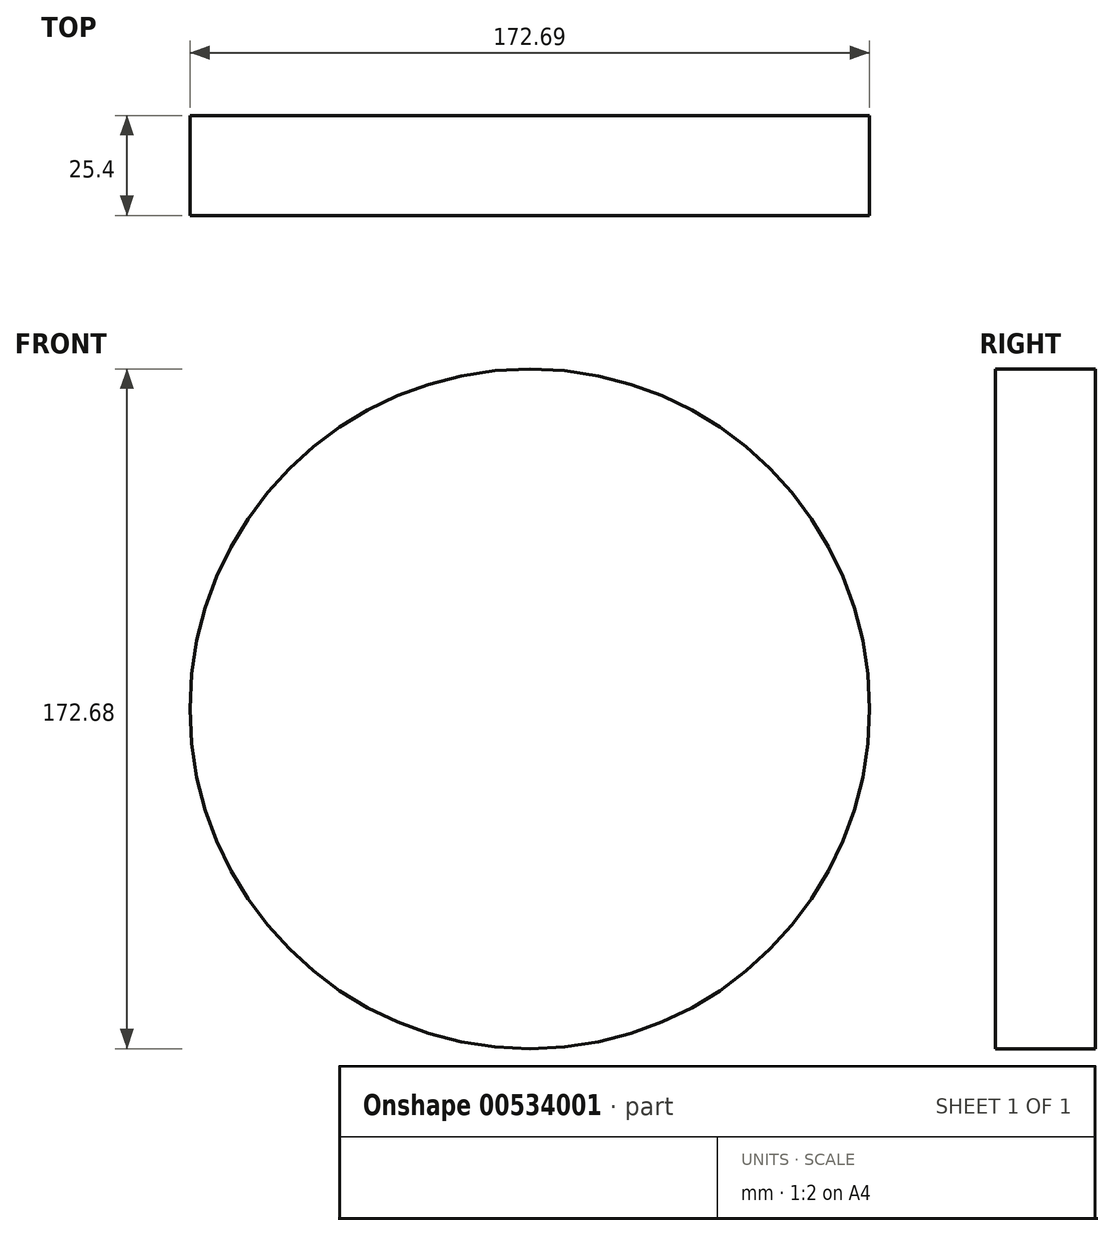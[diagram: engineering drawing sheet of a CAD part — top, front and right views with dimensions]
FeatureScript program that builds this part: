
annotation { "Feature Type Name" : "Feature", "Feature Type Description" : "" }
export const myFeature = defineFeature(function(context is Context, id is Id, definition is map)
    precondition{}
    {
        {
            var Q0;
            Q0=qCreatedBy(makeId("Front.planeOp"),FACE);
            var sketch = newSketch(context, id + "F0", { "sketchPlane" : qUnion([Q0])});
            skCircle(sketch, "E0", {"center": v(-25.18, 37.78) * mm, "radius": 86.34 * mm});
            skSolve(sketch);
        }
        {
            var Q0;
            Q0 = qSketchRegion(id + "F0", true);
            extrude(context, id + "F1", {"entities" : qUnion([Q0]), "depth" : 25.4 * mm, "offsetDistance" : 25.4 * mm});
        }
    });
